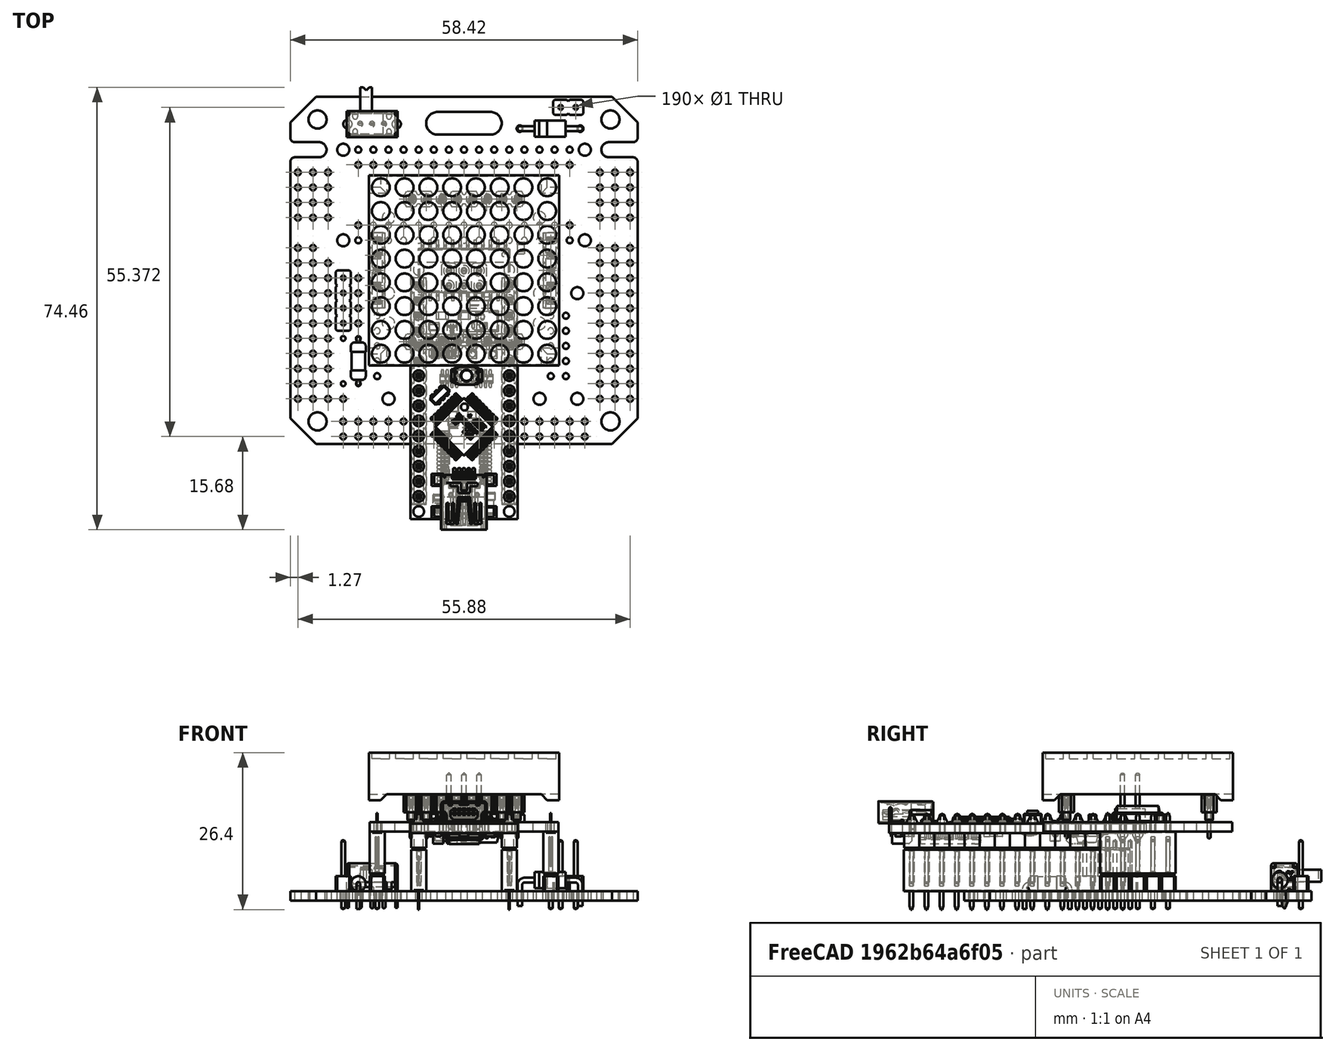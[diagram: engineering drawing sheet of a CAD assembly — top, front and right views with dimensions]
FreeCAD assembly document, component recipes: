
FREECAD ASSEMBLY — COMPONENT RECIPES ("BagTag_v3")

This assembly document has 9 components, labeled P0..P8 below (a component is one placed body or linked part). 8 of them carry a construction recipe — the FreeCAD feature program that regenerates the part from scratch, quoted from this document or its linked companion documents; the rest are supplied as boundary geometry only. No exploded tour is included for this assembly.
COMPONENT P0 — geometry summary ("BagTag"; no construction recipe available for this part):
  bounding box: 60.0 x 58.4 x 26.4 mm
  tessellated surface: 561,542 triangles
  volume: 9414 mm^3 (10% of its bounding box)
COMPONENT P1 — recipe-attached ("Body", modeled in this document).
Construction recipe (the document's own serialized feature program — sketch geometry with constraints, then the solid features built on it; lengths are millimeters unless a unit is written):

FEATURE [Sketcher::SketchObject] Sketch
  ArcFitTolerance = 0
  AttachmentSupport = -> [XY_Plane011]
  ExternalBSplineMaxDegree = 0
  ExternalBSplineTolerance = 0
  FullyConstrained = true
  InternalTolerance = 1e-06
  InvalidShape = false
  MakeInternals = false
  MapMode = 5
  Support = -> [XY_Plane011]
  TreeRank = 0
  ValidateShape = false
  sketch-geometry (2):
    g0: Circle CenterX=0 CenterY=0 CenterZ=0 NormalX=0 NormalY=0 NormalZ=1 AngleXU=0 Radius=38.5
    g1: Circle CenterX=0 CenterY=0 CenterZ=0 NormalX=0 NormalY=0 NormalZ=1 AngleXU=0 Radius=44.5
  constraints (4):
    c: Coincident(g0,g-1)
    c: Diameter(g0) = 77
    c: Diameter(g1) = 89
    c: Coincident(g1,g0)
FEATURE [PartDesign::Pad] Pad
  AddSubType = 0
  AutoTaperInnerAngle = false
  CheckUpToFaceLimits = true
  ClaimChildren = false
  Direction = (0,0,1)
  Fit = 0
  FitJoin = 0
  InnerFit = 0
  InnerFitJoin = 0
  InvalidShape = false
  Length = 24
  Length2 = 22
  NewSolid = false
  Profile = -> Sketch
  Suppress = false
  TaperInnerAngle = 0
  TaperInnerAngleRev = 0
  TreeRank = 0
  Type = 4
  ValidateShape = true
  _ProfileBasedVersion = 0
FEATURE [PartDesign::Body] Body
  AutoGroupSolids = false
  ClaimAllChildren = false
  ExportMode = 0
  Group = -> [Sketch,Pad]
  InvalidShape = false
  Origin = -> Origin011
  Tip = -> Pad
  TreeRank = 0
  ValidateShape = false
  _ExportChildren = -> [Pad]
  _GroupVersion = 1
COMPONENT P2 — recipe-attached ("Plate_bottom", modeled in this document).
Construction recipe (the document's own serialized feature program — sketch geometry with constraints, then the solid features built on it; lengths are millimeters unless a unit is written):

FEATURE [PartDesign::SubShapeBinder] Binder001
  BindCopyOnChange = 0
  BindMode = 0
  ClaimChildren = false
  Context = -> Body001 [Binder001.]
  EdgeTolerance = 1e-06
  FillStyle = 0
  Fuse = false
  InvalidShape = false
  MakeFace = true
  MergeEdges = true
  OffsetFill = false
  OffsetIntersection = false
  OffsetJoinType = 0
  OffsetOpenResult = false
  Outline = false
  PartialLoad = false
  Relative = true
  SplitEdges = false
  Support = -> [Board_fc76]
  TightBound = false
  TreeRank = 0
  ValidateShape = false
  _Version = 2
FEATURE [Sketcher::SketchObject] Sketch001
  ArcFitTolerance = 0
  AttachmentSupport = -> [XY_Plane020]
  ExternalBSplineMaxDegree = 0
  ExternalBSplineTolerance = 0
  ExternalGeometry = -> [Binder001]
  FullyConstrained = true
  InternalTolerance = 1e-06
  InvalidShape = false
  MakeInternals = false
  MapMode = 5
  Support = -> [XY_Plane020]
  TreeRank = 0
  ValidateShape = false
  sketch-geometry (22):
    g0: LineSegment StartX=-24.638 StartY=29.972 StartZ=0 EndX=24.638 EndY=29.972 EndZ=0
    g1: LineSegment StartX=29.21 StartY=25.4 StartZ=0 EndX=29.21 EndY=-41.456 EndZ=0
    g2: LineSegment StartX=24.638 StartY=-46.028 StartZ=0 EndX=-24.638 EndY=-46.028 EndZ=0
    g3: LineSegment StartX=-29.21 StartY=-41.456 StartZ=0 EndX=-29.21 EndY=25.4 EndZ=0
    g4: ArcOfCircle CenterX=-24.638 CenterY=25.4 CenterZ=0 NormalX=0 NormalY=0 NormalZ=1 AngleXU=0 Radius=4.572 StartAngle=1.5708 EndAngle=3.14159
    g5: GeomPoint [constr] X=-29.21 Y=29.972 Z=0
    g6: ArcOfCircle CenterX=24.638 CenterY=25.4 CenterZ=0 NormalX=0 NormalY=0 NormalZ=1 AngleXU=0 Radius=4.572 StartAngle=0 EndAngle=1.5708
    g7: GeomPoint [constr] X=29.21 Y=29.972 Z=0
    g8: ArcOfCircle CenterX=24.638 CenterY=-41.456 CenterZ=0 NormalX=0 NormalY=0 NormalZ=1 AngleXU=0 Radius=4.572 StartAngle=4.71239 EndAngle=6.28319
    g9: GeomPoint [constr] X=29.21 Y=-46.028 Z=0
    g10: ArcOfCircle CenterX=-24.638 CenterY=-41.456 CenterZ=0 NormalX=0 NormalY=0 NormalZ=1 AngleXU=0 Radius=4.572 StartAngle=3.14159 EndAngle=4.71239
    g11: GeomPoint [constr] X=-29.21 Y=-46.028 Z=0
    g12: Circle CenterX=-24.638 CenterY=-41.456 CenterZ=0 NormalX=0 NormalY=0 NormalZ=1 AngleXU=0 Radius=1.525
    g13: Circle CenterX=24.638 CenterY=-41.456 CenterZ=0 NormalX=0 NormalY=0 NormalZ=1 AngleXU=0 Radius=1.525
    g14: Circle CenterX=24.638 CenterY=25.4 CenterZ=0 NormalX=0 NormalY=0 NormalZ=1 AngleXU=0 Radius=1.525
    g15: Circle CenterX=-24.638 CenterY=25.4 CenterZ=0 NormalX=0 NormalY=0 NormalZ=1 AngleXU=0 Radius=1.525
    g16: ArcOfCircle CenterX=-4.445 CenterY=24.765 CenterZ=0 NormalX=0 NormalY=0 NormalZ=1 AngleXU=0 Radius=1.905 StartAngle=1.5708 EndAngle=4.71239
    g17: ArcOfCircle CenterX=4.445 CenterY=24.765 CenterZ=0 NormalX=0 NormalY=0 NormalZ=1 AngleXU=0 Radius=1.905 StartAngle=4.71239 EndAngle=7.85398
    g18: LineSegment StartX=-4.445 StartY=22.86 StartZ=0 EndX=4.445 EndY=22.86 EndZ=0
    g19: LineSegment StartX=-4.445 StartY=26.67 StartZ=0 EndX=4.445 EndY=26.67 EndZ=0
    g20: Circle CenterX=-24.638 CenterY=-25.4 CenterZ=0 NormalX=0 NormalY=0 NormalZ=1 AngleXU=0 Radius=1.525
    g21: Circle CenterX=24.638 CenterY=-25.4 CenterZ=0 NormalX=0 NormalY=0 NormalZ=1 AngleXU=0 Radius=1.525
  constraints (46):
    c: Horizontal(g0)
    c: Horizontal(g2)
    c: Vertical(g1)
    c: Vertical(g3)
    c: PointOnObject(g5,g0)
    c: PointOnObject(g5,g3)
    c: Tangent(g0,g4) = 1.5708
    c: Tangent(g3,g4) = 1.5708
    c: PointOnObject(g7,g0)
    c: PointOnObject(g7,g1)
    c: Tangent(g0,g6) = 1.5708
    c: Tangent(g1,g6) = 1.5708
    c: PointOnObject(g9,g1)
    c: PointOnObject(g9,g2)
    c: Tangent(g1,g8) = 1.5708
    c: Tangent(g2,g8) = 1.5708
    c: PointOnObject(g11,g3)
    c: PointOnObject(g11,g2)
    c: Tangent(g3,g10) = 1.5708
    c: Tangent(g2,g10) = 1.5708
    c: Equal(g10,g8)
    c: Equal(g8,g6)
    c: Coincident(g12,g10)
    c: Coincident(g13,g8)
    c: Coincident(g14,g6)
    c: Coincident(g15,g4)
    c: Equal(g15,g14)
    c: Equal(g14,g13)
    c: Equal(g13,g12)
    c: Tangent(g16,g19) = 1.5708
    c: Tangent(g16,g18) = -1.5708
    c: Tangent(g18,g17) = -1.5708
    c: Tangent(g19,g17) = 1.5708
    c: Horizontal(g18)
    c: Coincident(g4,g-3)
    c: Coincident(g-4,g6)
    c: PointOnObject(g-8,g1)
    c: Coincident(g20,g-5)
    c: Equal(g20,g15)
    c: Diameter(g15) = 3.05
    c: Coincident(g21,g-6)
    c: Equal(g21,g15)
    c: DistanceY(g2,g0) = 76
    c: Coincident(g16,g-9)
    c: Coincident(g17,g-10)
    c: Equal(g-9,g16)
FEATURE [PartDesign::Pad] Pad001
  AddSubType = 0
  AutoTaperInnerAngle = false
  CheckUpToFaceLimits = true
  ClaimChildren = false
  Direction = (0,0,1)
  Fit = 0
  FitJoin = 0
  InnerFit = 0
  InnerFitJoin = 0
  InvalidShape = false
  Length = 3
  Length2 = 100
  NewSolid = false
  Profile = -> Sketch001
  Reversed = true
  Suppress = false
  TaperInnerAngle = 0
  TaperInnerAngleRev = 0
  TreeRank = 0
  Type = 0
  ValidateShape = true
  _ProfileBasedVersion = 0
FEATURE [PartDesign::Body] Body001  label="Plate_bottom"
  AutoGroupSolids = false
  ClaimAllChildren = false
  ExportMode = 0
  Group = -> [Sketch001,Pad001,Binder001]
  InvalidShape = false
  Origin = -> Origin020
  Placement = pos=(0,0,-4.5) rot=(0,0,1;0rad)
  Tip = -> Pad001
  TreeRank = 0
  ValidateShape = false
  _ExportChildren = -> [Pad001,Binder001]
  _GroupVersion = 1
COMPONENT P3 — recipe-attached ("Spacer_bottom1", modeled in this document).
Construction recipe (the document's own serialized feature program — sketch geometry with constraints, then the solid features built on it; lengths are millimeters unless a unit is written):

FEATURE [PartDesign::SubShapeBinder] Binder
  BindCopyOnChange = 0
  BindMode = 0
  ClaimChildren = false
  Context = -> Group [Body002.Binder.]
  EdgeTolerance = 1e-06
  FillStyle = 0
  Fuse = false
  InvalidShape = false
  MakeFace = true
  MergeEdges = true
  OffsetFill = false
  OffsetIntersection = false
  OffsetJoinType = 0
  OffsetOpenResult = false
  Outline = false
  PartialLoad = false
  Relative = true
  SplitEdges = false
  Support = -> [Board_fc76]
  TightBound = false
  TreeRank = 0
  ValidateShape = false
  _Version = 2
FEATURE [Sketcher::SketchObject] Sketch002
  ArcFitTolerance = 0
  AttachmentSupport = -> [Binder]
  ExternalBSplineMaxDegree = 0
  ExternalBSplineTolerance = 0
  ExternalGeometry = -> [Binder]
  FullyConstrained = true
  InternalTolerance = 1e-06
  InvalidShape = false
  MakeInternals = false
  MapMode = 5
  Placement = pos=(0,0,-1.6) rot=(1,0,0;3.14159rad)
  Support = -> [Binder]
  TreeRank = 0
  ValidateShape = false
  sketch-geometry (2):
    g0: Circle CenterX=-24.638 CenterY=-25.4 CenterZ=0 NormalX=0 NormalY=0 NormalZ=1 AngleXU=0 Radius=1.525
    g1: Circle CenterX=-24.638 CenterY=-25.4 CenterZ=0 NormalX=0 NormalY=0 NormalZ=1 AngleXU=0 Radius=3
  constraints (6):
    c: Coincident(g1,g0)
    c: Coincident(g0,g-3)
    c: Diameter(g0) = 3.05
    c: Diameter(g1) = 6
    c: DistanceX(g0,g-4) = 49.276
    c: DistanceY(g-6,g-4) = -50.8
FEATURE [PartDesign::Pad] Pad002
  AddSubType = 0
  AutoTaperInnerAngle = false
  CheckUpToFaceLimits = true
  ClaimChildren = false
  Direction = (0,0,1)
  Fit = 0
  FitJoin = 0
  InnerFit = 0
  InnerFitJoin = 0
  InvalidShape = false
  Length = 3
  Length2 = 100
  NewSolid = false
  Profile = -> Sketch002
  Suppress = false
  TaperInnerAngle = 0
  TaperInnerAngleRev = 0
  TreeRank = 0
  Type = 0
  ValidateShape = true
  _ProfileBasedVersion = 0
FEATURE [PartDesign::Body] Body002  label="Spacer_bottom1"
  AutoGroupSolids = false
  ClaimAllChildren = false
  ExportMode = 0
  Group = -> [Sketch002,Pad002,Binder]
  InvalidShape = false
  Origin = -> Origin021
  Tip = -> Pad002
  TreeRank = 0
  ValidateShape = false
  _ExportChildren = -> [Pad002,Binder]
  _GroupVersion = 1
COMPONENT P4 — recipe-attached ("Plate_top", modeled in this document).
Construction recipe (the document's own serialized feature program — sketch geometry with constraints, then the solid features built on it; lengths are millimeters unless a unit is written):

FEATURE [PartDesign::SubShapeBinder] Binder002
  BindCopyOnChange = 0
  BindMode = 0
  ClaimChildren = false
  Context = -> Body003 [Binder002.]
  EdgeTolerance = 1e-06
  FillStyle = 0
  Fuse = false
  InvalidShape = false
  MakeFace = true
  MergeEdges = true
  OffsetFill = false
  OffsetIntersection = false
  OffsetJoinType = 0
  OffsetOpenResult = false
  Outline = false
  PartialLoad = false
  Relative = true
  SplitEdges = false
  Support = -> [Board_fc76]
  TightBound = false
  TreeRank = 0
  ValidateShape = false
  _Version = 2
FEATURE [PartDesign::SubShapeBinder] Binder003
  BindCopyOnChange = 0
  BindMode = 0
  ClaimChildren = false
  Context = -> Body003 [Binder003.]
  EdgeTolerance = 1e-06
  FillStyle = 0
  Fuse = false
  InvalidShape = false
  MakeFace = true
  MergeEdges = true
  OffsetFill = false
  OffsetIntersection = false
  OffsetJoinType = 0
  OffsetOpenResult = false
  Outline = false
  PartialLoad = false
  Relative = true
  SplitEdges = false
  Support = -> [Body001]
  TightBound = false
  TreeRank = 0
  ValidateShape = false
  _Version = 2
FEATURE [PartDesign::SubShapeBinder] Binder005  label="Binder005(M3x22xx5.5-Spacer033)"
  BindCopyOnChange = 0
  BindMode = 0
  ClaimChildren = false
  Context = -> Body003 [Binder005.]
  EdgeTolerance = 1e-06
  FillStyle = 0
  Fuse = false
  InvalidShape = false
  MakeFace = true
  MergeEdges = true
  OffsetFill = false
  OffsetIntersection = false
  OffsetJoinType = 0
  OffsetOpenResult = false
  Outline = false
  PartialLoad = false
  Relative = true
  SplitEdges = false
  Support = -> [Spacer]
  TightBound = false
  TreeRank = 1
  ValidateShape = false
  _Version = 8
FEATURE [Sketcher::SketchObject] Sketch003
  ArcFitTolerance = 0
  AttachmentSupport = -> [Binder005]
  ExternalBSplineMaxDegree = 0
  ExternalBSplineTolerance = 0
  ExternalGeometry = -> [Binder002,Binder003]
  FullyConstrained = true
  InternalTolerance = 1e-06
  InvalidShape = false
  MakeInternals = false
  MapMode = 5
  Placement = pos=(0,0,21.3) rot=(0,0,1;0rad)
  Support = -> [Binder005]
  TreeRank = 0
  ValidateShape = false
  sketch-geometry (42):
    g0: LineSegment StartX=-24.638 StartY=29.972 StartZ=0 EndX=24.638 EndY=29.972 EndZ=0
    g1: LineSegment StartX=29.21 StartY=25.4 StartZ=0 EndX=29.21 EndY=-41.456 EndZ=0
    g2: LineSegment StartX=24.638 StartY=-46.028 StartZ=0 EndX=-24.638 EndY=-46.028 EndZ=0
    g3: LineSegment StartX=-29.21 StartY=-41.456 StartZ=0 EndX=-29.21 EndY=25.4 EndZ=0
    g4: ArcOfCircle CenterX=-24.638 CenterY=25.4 CenterZ=0 NormalX=0 NormalY=0 NormalZ=1 AngleXU=0 Radius=4.572 StartAngle=1.5708 EndAngle=3.14159
    g5: GeomPoint [constr] X=-29.21 Y=29.972 Z=0
    g6: ArcOfCircle CenterX=24.638 CenterY=25.4 CenterZ=0 NormalX=0 NormalY=0 NormalZ=1 AngleXU=0 Radius=4.572 StartAngle=2e-16 EndAngle=1.5708
    g7: GeomPoint [constr] X=29.21 Y=29.972 Z=0
    g8: ArcOfCircle CenterX=24.638 CenterY=-41.456 CenterZ=0 NormalX=0 NormalY=0 NormalZ=1 AngleXU=0 Radius=4.572 StartAngle=4.71239 EndAngle=6.28319
    g9: GeomPoint [constr] X=29.21 Y=-46.028 Z=0
    g10: ArcOfCircle CenterX=-24.638 CenterY=-41.456 CenterZ=0 NormalX=0 NormalY=0 NormalZ=1 AngleXU=0 Radius=4.572 StartAngle=3.14159 EndAngle=4.71239
    g11: GeomPoint [constr] X=-29.21 Y=-46.028 Z=0
    g12: Circle CenterX=-24.638 CenterY=-41.456 CenterZ=0 NormalX=0 NormalY=0 NormalZ=1 AngleXU=0 Radius=1.525
    g13: Circle CenterX=24.638 CenterY=-41.456 CenterZ=0 NormalX=0 NormalY=0 NormalZ=1 AngleXU=0 Radius=1.525
    g14: Circle CenterX=24.638 CenterY=25.4 CenterZ=0 NormalX=0 NormalY=0 NormalZ=1 AngleXU=0 Radius=1.525
    g15: Circle CenterX=-24.638 CenterY=25.4 CenterZ=0 NormalX=0 NormalY=0 NormalZ=1 AngleXU=0 Radius=1.525
    g16: ArcOfCircle CenterX=-4.445 CenterY=24.765 CenterZ=0 NormalX=0 NormalY=0 NormalZ=1 AngleXU=0 Radius=1.905 StartAngle=1.5708 EndAngle=4.71239
    g17: ArcOfCircle CenterX=4.445 CenterY=24.765 CenterZ=0 NormalX=0 NormalY=0 NormalZ=1 AngleXU=0 Radius=1.905 StartAngle=4.71239 EndAngle=7.85398
    g18: LineSegment StartX=-4.445 StartY=22.86 StartZ=0 EndX=4.445 EndY=22.86 EndZ=0
    g19: LineSegment StartX=-4.445 StartY=26.67 StartZ=0 EndX=4.445 EndY=26.67 EndZ=0
    g20: ArcOfCircle CenterX=-16.0007 CenterY=3.30062 CenterZ=0 NormalX=0 NormalY=0 NormalZ=1 AngleXU=0 Radius=1 StartAngle=1.5708 EndAngle=3.14159
    g21: LineSegment StartX=-16.0007 StartY=4.30062 StartZ=0 EndX=15.9993 EndY=4.30062 EndZ=0
    g22: ArcOfCircle CenterX=15.9993 CenterY=3.30062 CenterZ=0 NormalX=0 NormalY=0 NormalZ=1 AngleXU=0 Radius=1 StartAngle=0 EndAngle=1.5708
    g23: LineSegment StartX=16.9993 StartY=3.30062 StartZ=0 EndX=16.9993 EndY=-28.6994 EndZ=0
    g24: ArcOfCircle CenterX=15.9993 CenterY=-28.6994 CenterZ=0 NormalX=0 NormalY=0 NormalZ=1 AngleXU=0 Radius=1 StartAngle=4.71239 EndAngle=6.28319
    g25: LineSegment StartX=15.9993 StartY=-29.6994 StartZ=0 EndX=-16.0007 EndY=-29.6994 EndZ=0
    g26: ArcOfCircle CenterX=-16.0007 CenterY=-28.6994 CenterZ=0 NormalX=0 NormalY=0 NormalZ=1 AngleXU=0 Radius=1 StartAngle=3.14159 EndAngle=4.71239
    g27: LineSegment StartX=-17.0007 StartY=-28.6994 StartZ=0 EndX=-17.0007 EndY=3.30062 EndZ=0
    g28: GeomPoint [constr] X=-17.0007 Y=4.30062 Z=0
    g29: GeomPoint [constr] X=16.9993 Y=-29.6994 Z=0
    g30: ArcOfCircle CenterX=17.023 CenterY=16.01 CenterZ=0 NormalX=0 NormalY=0 NormalZ=1 AngleXU=0 Radius=1 StartAngle=1.5708 EndAngle=3.14159
    g31: LineSegment StartX=17.023 StartY=17.01 StartZ=0 EndX=21.023 EndY=17.01 EndZ=0
    g32: ArcOfCircle CenterX=21.023 CenterY=16.01 CenterZ=0 NormalX=0 NormalY=0 NormalZ=1 AngleXU=0 Radius=1 StartAngle=8e-16 EndAngle=1.5708
    g33: LineSegment StartX=22.023 StartY=16.01 StartZ=0 EndX=22.023 EndY=9.39 EndZ=0
    g34: ArcOfCircle CenterX=21.023 CenterY=9.39 CenterZ=0 NormalX=0 NormalY=0 NormalZ=1 AngleXU=0 Radius=1 StartAngle=4.71239 EndAngle=6.28319
    g35: LineSegment StartX=21.023 StartY=8.39 StartZ=0 EndX=17.023 EndY=8.39 EndZ=0
    g36: ArcOfCircle CenterX=17.023 CenterY=9.39 CenterZ=0 NormalX=0 NormalY=0 NormalZ=1 AngleXU=0 Radius=1 StartAngle=3.14159 EndAngle=4.71239
    g37: LineSegment StartX=16.023 StartY=9.39 StartZ=0 EndX=16.023 EndY=16.01 EndZ=0
    g38: GeomPoint [constr] X=16.023 Y=17.01 Z=0
    g39: GeomPoint [constr] X=22.023 Y=8.39 Z=0
    g40: Circle CenterX=-24.638 CenterY=-25.4 CenterZ=0 NormalX=0 NormalY=0 NormalZ=1 AngleXU=0 Radius=1.525
    g41: Circle CenterX=24.638 CenterY=-25.4 CenterZ=0 NormalX=0 NormalY=0 NormalZ=1 AngleXU=0 Radius=1.525
  constraints (89):
    c: Horizontal(g0)
    c: Horizontal(g2)
    c: Vertical(g1)
    c: Vertical(g3)
    c: PointOnObject(g5,g0)
    c: PointOnObject(g5,g3)
    c: Tangent(g0,g4) = 1.5708
    c: Tangent(g3,g4) = 1.5708
    c: PointOnObject(g7,g0)
    c: PointOnObject(g7,g1)
    c: Tangent(g0,g6) = 1.5708
    c: Tangent(g1,g6) = 1.5708
    c: PointOnObject(g9,g1)
    c: PointOnObject(g9,g2)
    c: Tangent(g1,g8) = 1.5708
    c: Tangent(g2,g8) = 1.5708
    c: PointOnObject(g11,g2)
    c: PointOnObject(g11,g3)
    c: Tangent(g2,g10) = 1.5708
    c: Tangent(g3,g10) = 1.5708
    c: Equal(g10,g8)
    c: Coincident(g12,g10)
    c: Coincident(g13,g8)
    c: Coincident(g14,g6)
    c: Coincident(g15,g4)
    c: Equal(g15,g14)
    c: Equal(g14,g13)
    c: Equal(g13,g12)
    c: Tangent(g16,g19) = 1.5708
    c: Tangent(g16,g18) = -1.5708
    c: Tangent(g18,g17) = -1.5708
    c: Tangent(g19,g17) = 1.5708
    c: Horizontal(g18)
    c: Coincident(g16,g-7)
    c: Coincident(g17,g-8)
    c: Equal(g16,g-7)
    c: Coincident(g4,g-3)
    c: Coincident(g6,g-4)
    c: PointOnObject(g-9,g3)
    c: Coincident(g10,g-12)
    c: Diameter(g15) = 3.05
    c: Tangent(g20,g21) = 1.5708
    c: Tangent(g21,g22) = 1.5708
    c: Tangent(g22,g23) = 1.5708
    c: Tangent(g23,g24) = 1.5708
    c: Tangent(g24,g25) = 1.5708
    c: Tangent(g25,g26) = 1.5708
    c: Tangent(g26,g27) = 1.5708
    c: Tangent(g27,g20) = 1.5708
    c: Horizontal(g21)
    c: Horizontal(g25)
    c: Vertical(g23)
    c: Vertical(g27)
    c: Equal(g20,g22)
    c: Equal(g22,g24)
    c: Equal(g24,g26)
    c: PointOnObject(g28,g21)
    c: PointOnObject(g28,g27)
    c: PointOnObject(g29,g23)
    c: PointOnObject(g29,g25)
    c: Coincident(g20,g-19)
    c: Coincident(g24,g-20)
    c: DistanceY(g20,g20) = 1
    c: Tangent(g30,g31) = 1.5708
    c: Tangent(g31,g32) = 1.5708
    c: Tangent(g32,g33) = 1.5708
    c: Tangent(g33,g34) = 1.5708
    c: Tangent(g34,g35) = 1.5708
    c: Tangent(g35,g36) = 1.5708
    c: Tangent(g36,g37) = 1.5708
    c: Tangent(g37,g30) = 1.5708
    c: Horizontal(g31)
    c: Horizontal(g35)
    c: Vertical(g33)
    c: Vertical(g37)
    c: Equal(g30,g32)
    c: Equal(g32,g34)
    c: Equal(g34,g36)
    c: PointOnObject(g38,g31)
    c: PointOnObject(g38,g37)
    c: PointOnObject(g39,g33)
    c: PointOnObject(g39,g35)
    c: Coincident(g-17,g36)
    c: Coincident(g32,g-18)
    c: DistanceY(g30,g30) = 1
    c: Coincident(g40,g-6)
    c: Coincident(g41,g-5)
    c: Equal(g41,g40)
    c: Equal(g40,g15)
FEATURE [PartDesign::Pad] Pad003
  AddSubType = 0
  AutoTaperInnerAngle = false
  CheckUpToFaceLimits = true
  ClaimChildren = false
  Direction = (0,0,1)
  Fit = 0
  FitJoin = 0
  InnerFit = 0
  InnerFitJoin = 0
  InvalidShape = false
  Length = 3
  Length2 = 100
  NewSolid = false
  Profile = -> Sketch003
  Suppress = false
  TaperInnerAngle = 0
  TaperInnerAngleRev = 0
  TreeRank = 0
  Type = 0
  ValidateShape = true
  _ProfileBasedVersion = 0
FEATURE [PartDesign::Body] Body003  label="Plate_top"
  AutoGroupSolids = false
  ClaimAllChildren = false
  ExportMode = 0
  Group = -> [Sketch003,Pad003,Binder002,Binder003,Binder005]
  InvalidShape = false
  Origin = -> Origin013
  Placement = pos=(0,0,0.6) rot=(0,0,1;0rad)
  Tip = -> Pad003
  TreeRank = 0
  ValidateShape = false
  _ExportChildren = -> [Pad003,Binder002,Binder003,Binder005]
  _GroupVersion = 1
COMPONENT P5 — recipe-attached ("Spacer_top", modeled in this document).
Construction recipe (the document's own serialized feature program — sketch geometry with constraints, then the solid features built on it; lengths are millimeters unless a unit is written):

FEATURE [PartDesign::SubShapeBinder] Binder004
  BindCopyOnChange = 0
  BindMode = 0
  ClaimChildren = false
  Context = -> Body005 [Binder004.]
  EdgeTolerance = 1e-06
  FillStyle = 0
  Fuse = false
  InvalidShape = false
  MakeFace = true
  MergeEdges = true
  OffsetFill = false
  OffsetIntersection = false
  OffsetJoinType = 0
  OffsetOpenResult = false
  Outline = false
  PartialLoad = false
  Relative = true
  SplitEdges = false
  Support = -> [Spacer]
  TightBound = false
  TreeRank = 0
  ValidateShape = false
  _Version = 2
FEATURE [Sketcher::SketchObject] Sketch005
  ArcFitTolerance = 0
  AttachmentSupport = -> [Binder004]
  ExternalBSplineMaxDegree = 0
  ExternalBSplineTolerance = 0
  ExternalGeometry = -> [Binder004]
  FullyConstrained = true
  InternalTolerance = 1e-06
  InvalidShape = false
  MakeInternals = false
  MapMode = 5
  Placement = pos=(0,0,21.9) rot=(0,0,1;0rad)
  Support = -> [Binder004]
  TreeRank = 0
  ValidateShape = false
  sketch-geometry (2):
    g0: Circle CenterX=-24.638 CenterY=-25.4 CenterZ=0 NormalX=0 NormalY=0 NormalZ=1 AngleXU=0 Radius=1.525
    g1: Circle CenterX=-24.638 CenterY=-25.4 CenterZ=0 NormalX=0 NormalY=0 NormalZ=1 AngleXU=0 Radius=3
  constraints (4):
    c: Coincident(g1,g0)
    c: Diameter(g0) = 3.05
    c: Diameter(g1) = 6
    c: Coincident(g-3,g0)
FEATURE [PartDesign::Pad] Pad004
  AddSubType = 0
  AutoTaperInnerAngle = false
  CheckUpToFaceLimits = true
  ClaimChildren = false
  Direction = (0,0,1)
  Fit = 0
  FitJoin = 0
  InnerFit = 0
  InnerFitJoin = 0
  InvalidShape = false
  Length = 3
  Length2 = 10
  NewSolid = false
  Profile = -> Sketch005
  Suppress = false
  TaperInnerAngle = 0
  TaperInnerAngleRev = 0
  TreeRank = 0
  Type = 0
  ValidateShape = true
  _ProfileBasedVersion = 0
FEATURE [PartDesign::Body] Body005  label="Spacer_top"
  AutoGroupSolids = false
  ClaimAllChildren = false
  ExportMode = 0
  Group = -> [Sketch005,Binder004,Pad004]
  InvalidShape = false
  Origin = -> Origin014
  Tip = -> Pad004
  TreeRank = 0
  ValidateShape = false
  _ExportChildren = -> [Binder004,Pad004]
  _GroupVersion = 1
COMPONENT P6 — recipe-attached ("Spacer_bottom2", modeled in this document).
Construction recipe (the document's own serialized feature program — sketch geometry with constraints, then the solid features built on it; lengths are millimeters unless a unit is written):

FEATURE [PartDesign::FeatureBase] Clone
  BaseFeature = -> Body002
  InvalidShape = false
  NewSolid = false
  Placement = pos=(0,0,4e-16) rot=(0,0,1;0rad)
  Suppress = false
  TreeRank = 0
  ValidateShape = true
FEATURE [PartDesign::Body] Body006  label="Spacer_bottom2"
  AutoGroupSolids = false
  BaseFeature = -> Body002
  ClaimAllChildren = false
  ExportMode = 0
  Group = -> [Clone]
  InvalidShape = false
  Origin = -> Origin022
  Placement = pos=(49.28,0,0) rot=(0,0,1;0rad)
  Tip = -> Clone
  TreeRank = 0
  ValidateShape = false
  _ExportChildren = -> [Clone]
  _GroupVersion = 1
COMPONENT P7 — recipe-attached ("Spacer_bottom3", modeled in this document).
Construction recipe (the document's own serialized feature program — sketch geometry with constraints, then the solid features built on it; lengths are millimeters unless a unit is written):

FEATURE [PartDesign::FeatureBase] Clone001
  BaseFeature = -> Body002
  InvalidShape = false
  NewSolid = false
  Placement = pos=(0,0,4e-16) rot=(0,0,1;0rad)
  Suppress = false
  TreeRank = 0
  ValidateShape = true
FEATURE [PartDesign::Body] Body007  label="Spacer_bottom3"
  AutoGroupSolids = false
  BaseFeature = -> Body002
  ClaimAllChildren = false
  ExportMode = 0
  Group = -> [Clone001]
  InvalidShape = false
  Origin = -> Origin023
  Placement = pos=(49.28,-50.8,0) rot=(0,0,1;0rad)
  Tip = -> Clone001
  TreeRank = 0
  ValidateShape = false
  _ExportChildren = -> [Clone001]
  _GroupVersion = 1
COMPONENT P8 — recipe-attached ("Spacer_bottom4", modeled in this document).
Construction recipe (the document's own serialized feature program — sketch geometry with constraints, then the solid features built on it; lengths are millimeters unless a unit is written):

FEATURE [PartDesign::FeatureBase] Clone002
  BaseFeature = -> Body002
  InvalidShape = false
  NewSolid = false
  Placement = pos=(0,0,4e-16) rot=(0,0,1;0rad)
  Suppress = false
  TreeRank = 0
  ValidateShape = true
FEATURE [PartDesign::Body] Body008  label="Spacer_bottom4"
  AutoGroupSolids = false
  BaseFeature = -> Body002
  ClaimAllChildren = false
  ExportMode = 0
  Group = -> [Clone002]
  InvalidShape = false
  Origin = -> Origin024
  Placement = pos=(0,-50.8,0) rot=(0,0,1;0rad)
  Tip = -> Clone002
  TreeRank = 0
  ValidateShape = false
  _ExportChildren = -> [Clone002]
  _GroupVersion = 1
PROVENANCE & LICENSES
A FreeCAD (.FCStd) document from a public repository crawl; recipes are the document's own serialized feature recipes (and, for linked parts, companion documents' recipes).
License: gpl-3.0.
